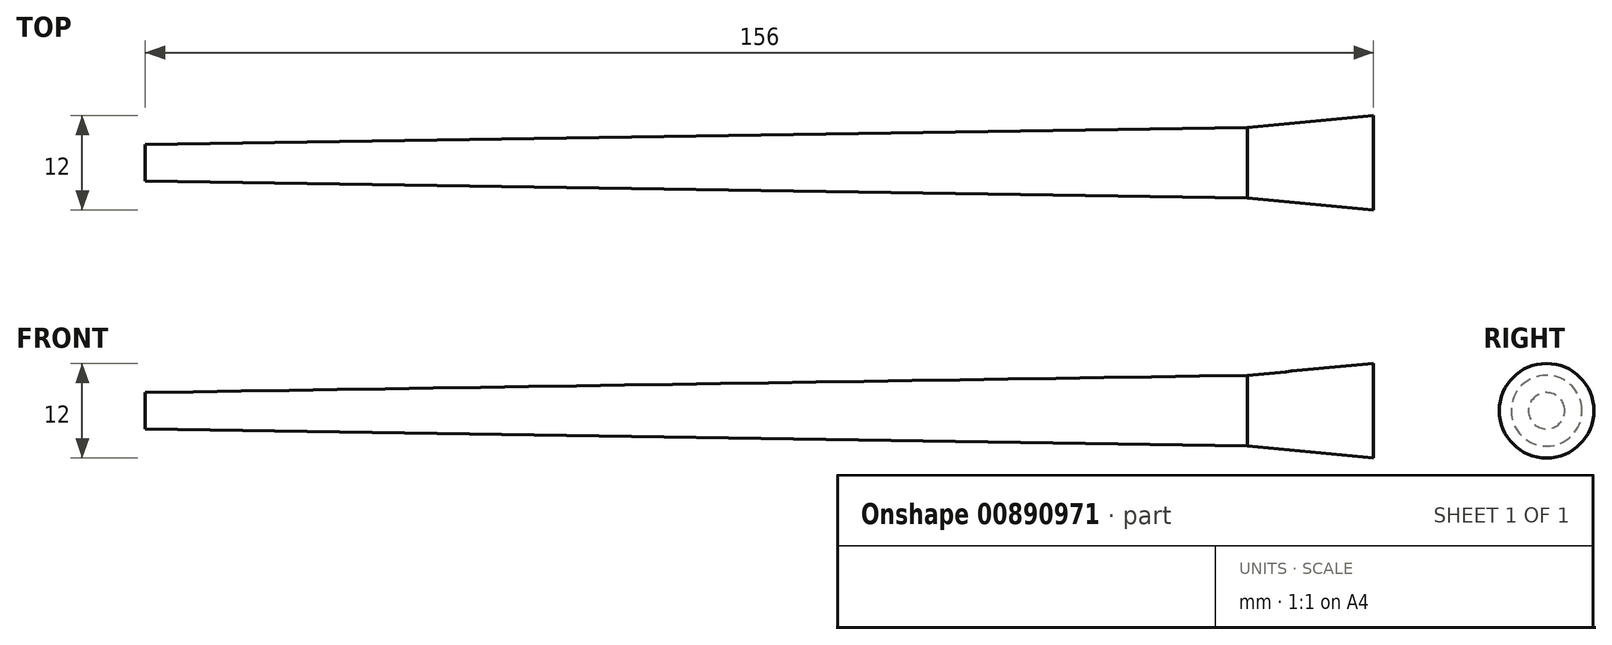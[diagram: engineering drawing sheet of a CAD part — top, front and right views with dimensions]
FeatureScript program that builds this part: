
annotation { "Feature Type Name" : "Feature", "Feature Type Description" : "" }
export const myFeature = defineFeature(function(context is Context, id is Id, definition is map)
    precondition{}
    {
        {
            var Q0;
            Q0=qCreatedBy(makeId("Top.planeOp"),FACE);
            var sketch = newSketch(context, id + "F0", { "sketchPlane" : qUnion([Q0])});
            skLineSegment(sketch, "E0.bottom", {"start": v(-94.05, 0) * mm, "end": v(45.95, 0) * mm});
            skLineSegment(sketch, "E0.left", {"start": v(-94.05, 0) * mm, "end": v(-94.05, 2.3) * mm});
            skLineSegment(sketch, "E0.right", {"start": v(45.95, 0) * mm, "end": v(45.95, 4.5) * mm});
            skLineSegment(sketch, "E1", {"start": v(-113.5, 0) * mm, "end": v(98.19, 0) * mm});
            skLineSegment(sketch, "E2", {"start": v(45.95, 4.5) * mm, "end": v(61.95, 6) * mm});
            skLineSegment(sketch, "E3", {"start": v(61.95, 6) * mm, "end": v(61.95, 0) * mm});
            skLineSegment(sketch, "E4", {"start": v(61.95, 0) * mm, "end": v(45.95, 0) * mm});
            skLineSegment(sketch, "E5", {"start": v(45.95, 4.5) * mm, "end": v(-94.05, 2.3) * mm});
            skPoint(sketch, "E0.top.start.orphan", {"position": v(-94.05, 4.6) * mm});
            skSolve(sketch);
        }
        {
            var Q0;
            Q0=qSketchRegion(id+"F0",true);
            var Q1;
            Q1=sQuery(id+"F0.wireOp",EDGE,"E1");
            revolve(context, id + "F1", {"surfaceOperationType" : NewSurfaceOperationType.NEW, "entities" : qUnion([Q0]), "axis" : qUnion([Q1]), "revolveType" : RevolveType.FULL});
        }
    });
